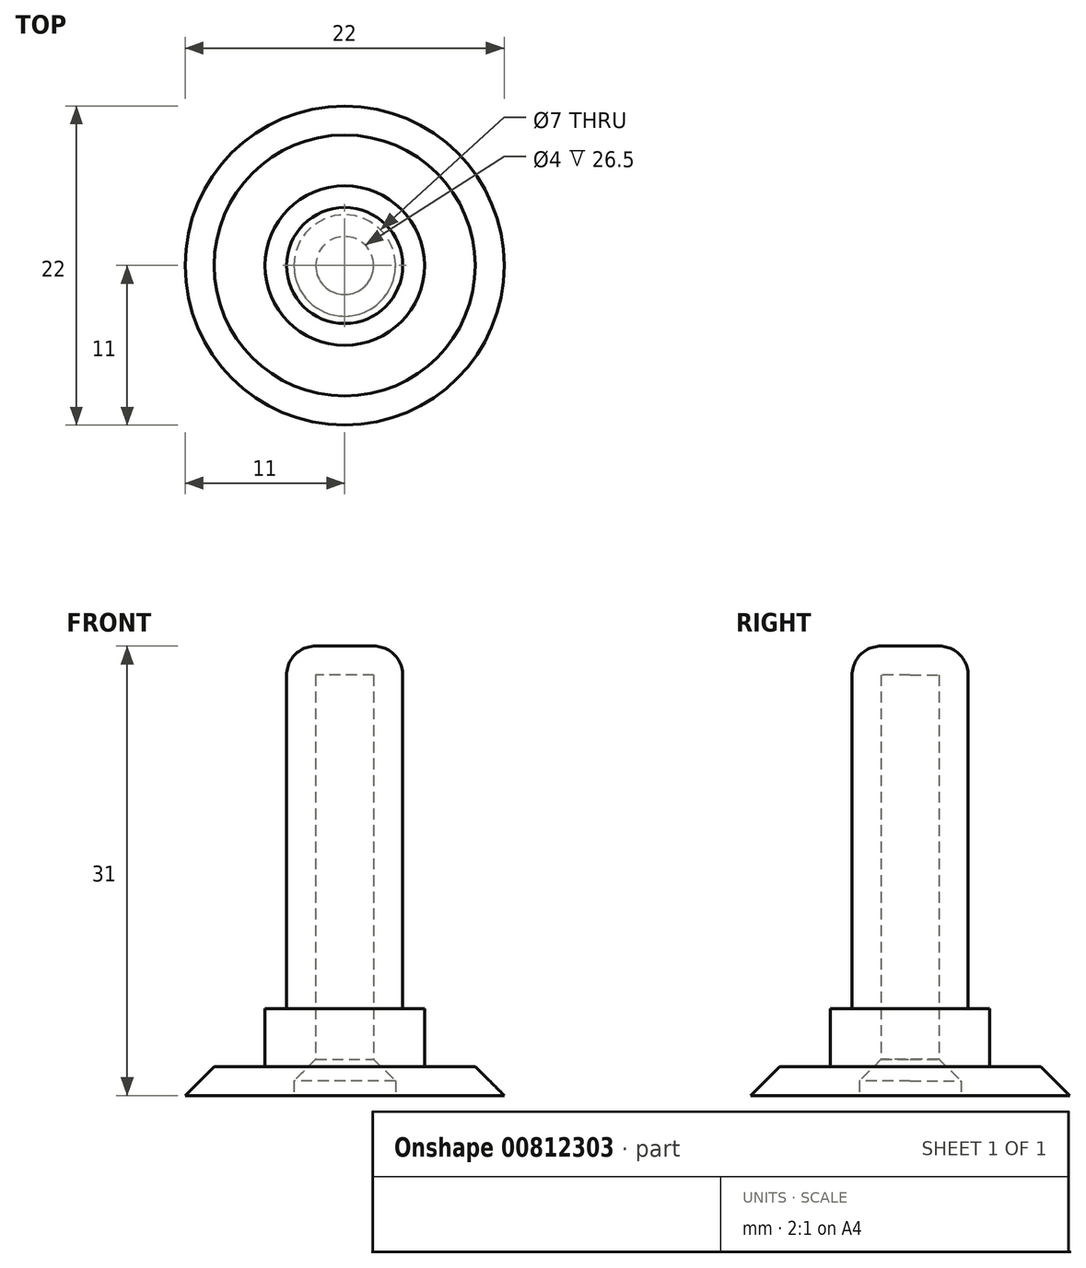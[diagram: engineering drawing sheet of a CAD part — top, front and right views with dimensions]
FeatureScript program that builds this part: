
annotation { "Feature Type Name" : "Feature", "Feature Type Description" : "" }
export const myFeature = defineFeature(function(context is Context, id is Id, definition is map)
    precondition{}
    {
        {
            var Q0;
            Q0=qCreatedBy(makeId("Top.planeOp"),FACE);
            var sketch = newSketch(context, id + "F0", { "sketchPlane" : qUnion([Q0])});
            skCircle(sketch, "E0", {"center": v(0, 0) * mm, "radius": 11 * mm});
            skSolve(sketch);
        }
        {
            var Q0;
            Q0=makeQuery(id+"F0.imprint","IMPRINT",FACE,{"disambiguationData":[TD([[makeQuery(id+"F0.imprint","IMPRINT",EDGE,{"derivedFrom":sQuery(id+"F0.wireOp",EDGE,"E0")}),1.0]])]});
            extrude(context, id + "F1", {"entities" : qUnion([Q0]), "depth" : 2 * mm, "offsetDistance" : 25 * mm});
        }
        {
            var Q0;
            Q0=makeQuery(id+"F1.opExtrude","CAP_FACE",FACE,{"disambiguationData":[OSD([sQuery(id+"F0.wireOp",EDGE,"E0")])],"isStart":false});
            var sketch = newSketch(context, id + "F2", { "sketchPlane" : qUnion([Q0])});
            skCircle(sketch, "E1", {"center": v(0, 0) * mm, "radius": 5.5 * mm});
            skSolve(sketch);
        }
        {
            var Q0;
            Q0=makeQuery(id+"F2.imprint","IMPRINT",FACE,{"disambiguationData":[TD([[makeQuery(id+"F2.imprint","IMPRINT",EDGE,{"derivedFrom":sQuery(id+"F2.wireOp",EDGE,"E1")}),1.0]])]});
            extrude(context, id + "F3", {"entities" : qUnion([Q0]), "operationType" : NewBodyOperationType.ADD, "depth" : 4 * mm, "offsetDistance" : 25 * mm});
        }
        {
            var Q0;
            Q0=makeQuery(id+"F3.opExtrude","CAP_FACE",FACE,{"disambiguationData":[OSD([sQuery(id+"F2.wireOp",EDGE,"E1")])],"isStart":false});
            var sketch = newSketch(context, id + "F4", { "sketchPlane" : qUnion([Q0])});
            skCircle(sketch, "E2", {"center": v(0, 0) * mm, "radius": 4 * mm});
            skSolve(sketch);
        }
        {
            var Q0;
            Q0 = qSketchRegion(id + "F4", true);
            extrude(context, id + "F5", {"entities" : qUnion([Q0]), "operationType" : NewBodyOperationType.ADD, "depth" : 25 * mm, "offsetDistance" : 25 * mm});
        }
        {
            var Q0;
            Q0=makeQuery(id+"F5.opExtrude","CAP_EDGE",EDGE,{"disambiguationData":[OSD([sQuery(id+"F4.wireOp",EDGE,"E2")])],"isStart":false});
            fillet(context, id + "F6", {"entities" : qUnion([Q0]), "radius" : 2 * mm, "tangentPropagation" : true, "allowEdgeOverflow" : false});
        }
        {
            var Q0;
            Q0=makeQuery(id+"F1.opExtrude","CAP_EDGE",EDGE,{"disambiguationData":[OSD([sQuery(id+"F0.wireOp",EDGE,"E0")])],"isStart":false});
            chamfer(context, id + "F7", {"entities" : qUnion([Q0]), "width" : 2 * mm, "tangentPropagation" : true});
        }
        {
            var Q0;
            Q0=makeQuery(id+"F1.opExtrude","CAP_FACE",FACE,{"disambiguationData":[OSD([sQuery(id+"F0.wireOp",EDGE,"E0")])],"isStart":true});
            shell(context, id + "F8", {"entities" : qUnion([Q0]), "thickness" : 2 * mm});
        }
        {
            var Q0;
            {var subQ0=sQuery(id+"F2.wireOp",EDGE,"E1");Q0=makeQuery(id+"F8.opShell","OFFSET_EDGE",EDGE,{"disambiguationData":[OSD([subQ0]),TDD([makeQuery(id+"F3.opExtrude","CAP_EDGE",EDGE,{"disambiguationData":[OSD([subQ0])],"isStart":true})])]});}
            chamfer(context, id + "F9", {"entities" : qUnion([Q0]), "width" : 3 * mm, "tangentPropagation" : true});
        }
    });
